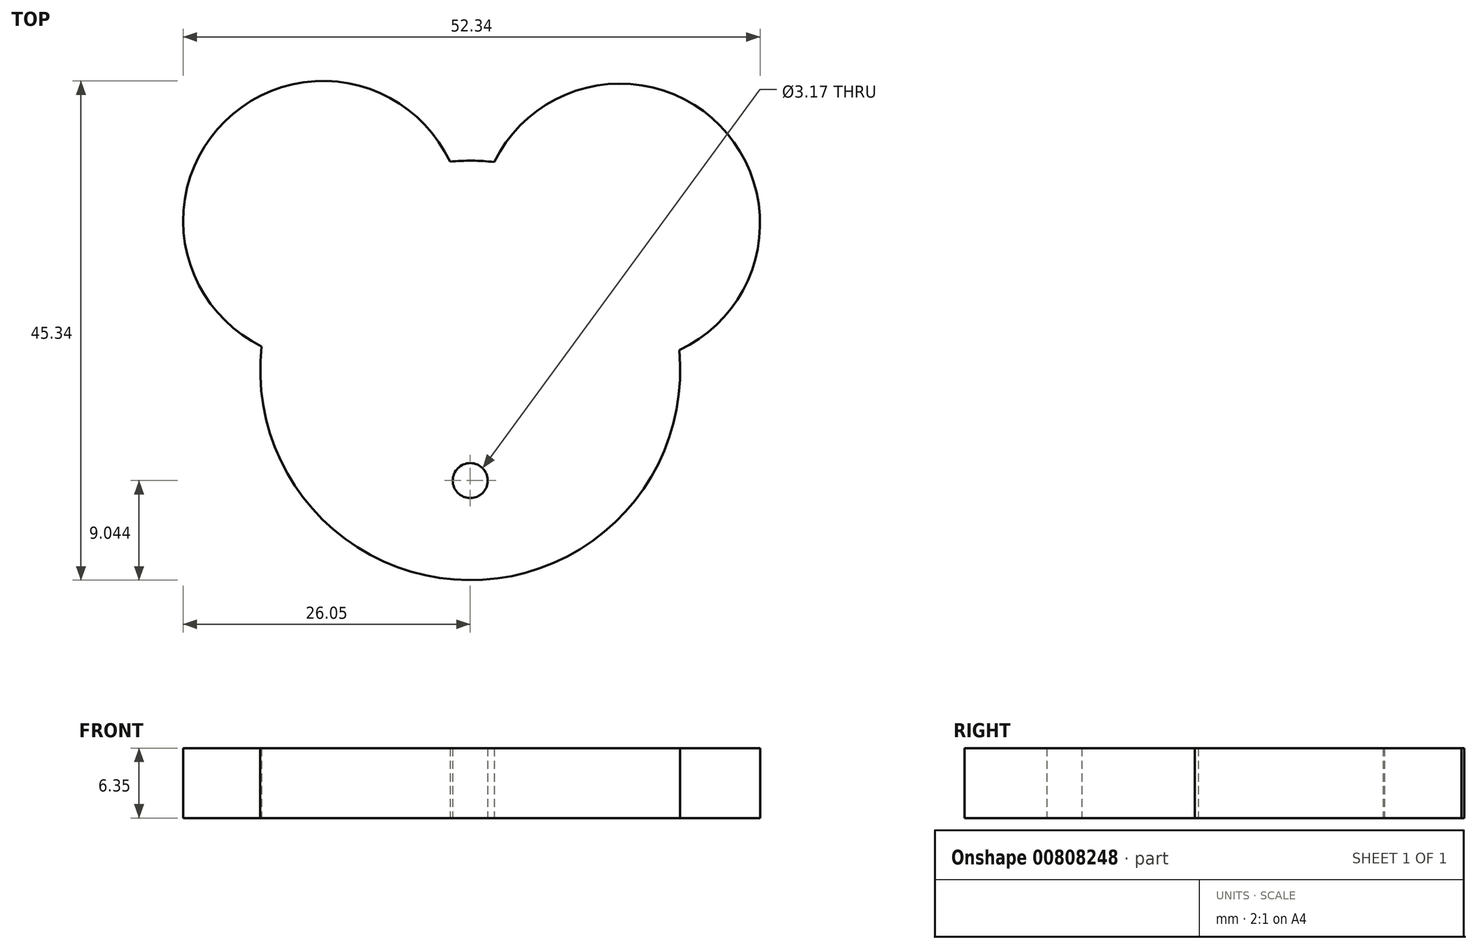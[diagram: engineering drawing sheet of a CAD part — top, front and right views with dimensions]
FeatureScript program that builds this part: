
annotation { "Feature Type Name" : "Feature", "Feature Type Description" : "" }
export const myFeature = defineFeature(function(context is Context, id is Id, definition is map)
    precondition{}
    {
        {
            var Q0;
            Q0=qCreatedBy(makeId("Top.planeOp"),FACE);
            var sketch = newSketch(context, id + "F0", { "sketchPlane" : qUnion([Q0])});
            skCircle(sketch, "E0", {"center": v(0, 0) * mm, "radius": 19.05 * mm});
            skLineSegment(sketch, "E1", {"start": v(0, 0) * mm, "end": v(-13.35, 13.6) * mm, "construction": true});
            skLineSegment(sketch, "E2", {"start": v(0, 0) * mm, "end": v(13.6, 13.35) * mm, "construction": true});
            skCircle(sketch, "E3", {"center": v(-13.35, 13.6) * mm, "radius": 12.7 * mm});
            skCircle(sketch, "E4", {"center": v(13.6, 13.35) * mm, "radius": 12.7 * mm});
            skSolve(sketch);
        }
        {
            var Q0;
            {var subQ0=sQuery(id+"F0.wireOp",EDGE,"E3");var subQ1=sQuery(id+"F0.wireOp",EDGE,"E0");var subQ2=makeQuery(id+"F0.imprint","INTERSECT",VERTEX,{"disambiguationData":[OD(0.0)],"derivedFrom":[subQ1,subQ0]});Q0=makeQuery(id+"F0.imprint","IMPRINT",FACE,{"disambiguationData":[TD([[makeQuery(id+"F0.imprint","IMPRINT",EDGE,{"disambiguationData":[TD([[subQ2,-1.0]])],"derivedFrom":subQ1}),-1.0]])]});}
            var Q1;
            {var subQ0=sQuery(id+"F0.wireOp",EDGE,"E3");var subQ1=sQuery(id+"F0.wireOp",EDGE,"E0");var subQ2=makeQuery(id+"F0.imprint","INTERSECT",VERTEX,{"disambiguationData":[OD(0.0)],"derivedFrom":[subQ1,subQ0]});Q1=makeQuery(id+"F0.imprint","IMPRINT",FACE,{"disambiguationData":[TD([[makeQuery(id+"F0.imprint","IMPRINT",EDGE,{"disambiguationData":[TD([[subQ2,-1.0]])],"derivedFrom":subQ1}),1.0]])]});}
            var Q2;
            {var subQ0=sQuery(id+"F0.wireOp",EDGE,"E4");var subQ1=sQuery(id+"F0.wireOp",EDGE,"E0");var subQ2=makeQuery(id+"F0.imprint","INTERSECT",VERTEX,{"disambiguationData":[OD(0.0)],"derivedFrom":[subQ1,subQ0]});Q2=makeQuery(id+"F0.imprint","IMPRINT",FACE,{"disambiguationData":[TD([[makeQuery(id+"F0.imprint","IMPRINT",EDGE,{"disambiguationData":[TD([[subQ2,1.0]])],"derivedFrom":subQ1}),1.0]])]});}
            var Q3;
            {var subQ0=sQuery(id+"F0.wireOp",EDGE,"E4");var subQ1=sQuery(id+"F0.wireOp",EDGE,"E0");var subQ2=makeQuery(id+"F0.imprint","INTERSECT",VERTEX,{"disambiguationData":[OD(0.0)],"derivedFrom":[subQ1,subQ0]});Q3=makeQuery(id+"F0.imprint","IMPRINT",FACE,{"disambiguationData":[TD([[makeQuery(id+"F0.imprint","IMPRINT",EDGE,{"disambiguationData":[TD([[subQ2,1.0]])],"derivedFrom":subQ1}),-1.0]])]});}
            var Q4;
            {var subQ0=sQuery(id+"F0.wireOp",EDGE,"E4");var subQ1=sQuery(id+"F0.wireOp",EDGE,"E0");var subQ2=makeQuery(id+"F0.imprint","INTERSECT",VERTEX,{"disambiguationData":[OD(0.0)],"derivedFrom":[subQ1,subQ0]});Q4=makeQuery(id+"F0.imprint","IMPRINT",FACE,{"disambiguationData":[TD([[makeQuery(id+"F0.imprint","IMPRINT",EDGE,{"disambiguationData":[TD([[subQ2,-1.0]])],"derivedFrom":subQ1}),1.0]])]});}
            extrude(context, id + "F1", {"entities" : qUnion([Q0, Q1, Q2, Q3, Q4]), "depth" : 6.35 * mm, "offsetDistance" : 25.4 * mm});
        }
        {
            var Q0;
            Q0=makeQuery(id+"F1.opExtrude","CAP_FACE",FACE,{"disambiguationData":[OSD([sQuery(id+"F0.wireOp",EDGE,"E0"),sQuery(id+"F0.wireOp",EDGE,"E3"),sQuery(id+"F0.wireOp",EDGE,"E4")])],"isStart":true});
            var sketch = newSketch(context, id + "F2", { "sketchPlane" : qUnion([Q0])});
            skCircle(sketch, "E5", {"center": v(0, 10) * mm, "radius": 1.59 * mm});
            skSolve(sketch);
        }
        {
            var Q0;
            Q0 = qSketchRegion(id + "F2", true);
            extrude(context, id + "F3", {"entities" : qUnion([Q0]), "operationType" : NewBodyOperationType.REMOVE, "endBound" : BoundingType.UP_TO_NEXT, "oppositeDirection" : true, "depth" : 25.4 * mm, "offsetDistance" : 25.4 * mm});
        }
    });
